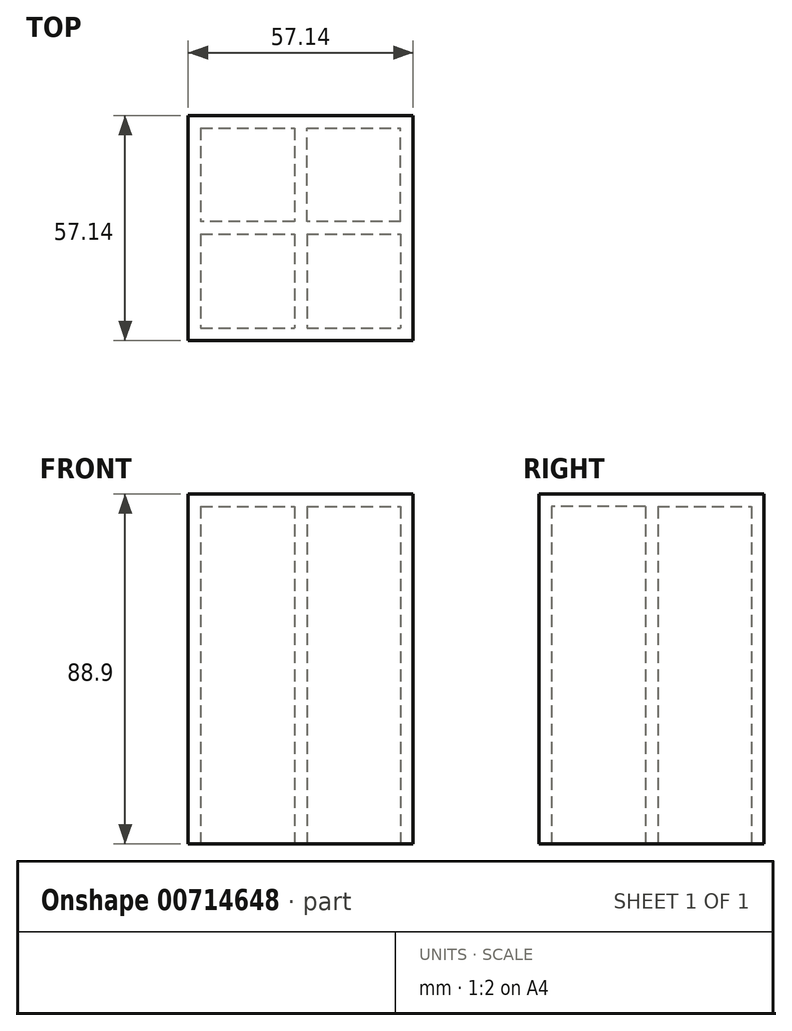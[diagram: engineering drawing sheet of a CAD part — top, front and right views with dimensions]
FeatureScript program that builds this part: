
annotation { "Feature Type Name" : "Feature", "Feature Type Description" : "" }
export const myFeature = defineFeature(function(context is Context, id is Id, definition is map)
    precondition{}
    {
        {
            var Q0;
            Q0=qCreatedBy(makeId("Top.planeOp"),FACE);
            var sketch = newSketch(context, id + "F0", { "sketchPlane" : qUnion([Q0])});
            skLineSegment(sketch, "E0.bottom", {"start": v(28.57, 28.58) * mm, "end": v(-28.58, 28.58) * mm});
            skLineSegment(sketch, "E0.top", {"start": v(28.58, -28.58) * mm, "end": v(-28.57, -28.58) * mm});
            skLineSegment(sketch, "E0.left", {"start": v(28.57, 28.58) * mm, "end": v(28.58, -28.58) * mm});
            skLineSegment(sketch, "E0.right", {"start": v(-28.58, 28.58) * mm, "end": v(-28.57, -28.58) * mm});
            skPoint(sketch, "E0.middle", {"position": v(0, 0) * mm});
            skSolve(sketch);
        }
        {
            var Q0;
            Q0=makeQuery(id+"F0.imprint","IMPRINT",FACE,{"disambiguationData":[TD([[makeQuery(id+"F0.imprint","IMPRINT",EDGE,{"derivedFrom":sQuery(id+"F0.wireOp",EDGE,"E0.bottom")}),1.0]])]});
            extrude(context, id + "F1", {"entities" : qUnion([Q0]), "depth" : 88.9 * mm, "offsetDistance" : 25.4 * mm});
        }
        {
            var Q0;
            Q0=qCreatedBy(makeId("Top.planeOp"),FACE);
            var sketch = newSketch(context, id + "F2", { "sketchPlane" : qUnion([Q0])});
            skLineSegment(sketch, "E1.bottom", {"start": v(-25.4, 25.4) * mm, "end": v(-1.59, 25.4) * mm});
            skLineSegment(sketch, "E1.left", {"start": v(-25.4, 25.4) * mm, "end": v(-25.4, 1.59) * mm});
            skLineSegment(sketch, "E1.right", {"start": v(-1.59, 25.4) * mm, "end": v(-1.59, 1.59) * mm});
            skLineSegment(sketch, "E2.top", {"start": v(1.59, 25.4) * mm, "end": v(25.4, 25.4) * mm});
            skLineSegment(sketch, "E2.left", {"start": v(1.59, 1.59) * mm, "end": v(1.59, 25.4) * mm});
            skLineSegment(sketch, "E2.right", {"start": v(25.4, 1.59) * mm, "end": v(25.4, 25.4) * mm});
            skLineSegment(sketch, "E3.bottom", {"start": v(-25.4, -1.59) * mm, "end": v(-1.59, -1.59) * mm});
            skLineSegment(sketch, "E3.top", {"start": v(-25.4, -25.4) * mm, "end": v(-1.59, -25.4) * mm});
            skLineSegment(sketch, "E3.left", {"start": v(-25.4, -1.59) * mm, "end": v(-25.4, -25.4) * mm});
            skLineSegment(sketch, "E3.right", {"start": v(-1.59, -1.59) * mm, "end": v(-1.59, -25.4) * mm});
            skLineSegment(sketch, "E4.bottom", {"start": v(1.59, -1.59) * mm, "end": v(25.4, -1.59) * mm});
            skLineSegment(sketch, "E4.top", {"start": v(1.59, -25.4) * mm, "end": v(25.4, -25.4) * mm});
            skLineSegment(sketch, "E4.right", {"start": v(25.4, -1.59) * mm, "end": v(25.4, -25.4) * mm});
            skLineSegment(sketch, "E5", {"start": v(25.4, 1.59) * mm, "end": v(1.59, 1.59) * mm});
            skPoint(sketch, "E6.orphan", {"position": v(1.59, 0) * mm});
            skLineSegment(sketch, "E7.trimOffspring", {"start": v(-1.59, 1.59) * mm, "end": v(-25.4, 1.59) * mm});
            skPoint(sketch, "E1.top.end.orphan", {"position": v(-1.59, 0) * mm});
            skLineSegment(sketch, "E8", {"start": v(0, 0) * mm, "end": v(0, 28.84) * mm});
            skLineSegment(sketch, "E9", {"start": v(1.59, -1.59) * mm, "end": v(1.59, -25.4) * mm});
            skSolve(sketch);
        }
        {
            var Q0;
            Q0=makeQuery(id+"F2.imprint","IMPRINT",FACE,{"disambiguationData":[TD([[makeQuery(id+"F2.imprint","IMPRINT",EDGE,{"derivedFrom":sQuery(id+"F2.wireOp",EDGE,"E3.bottom")}),-1.0]])]});
            var Q1;
            Q1=makeQuery(id+"F2.imprint","IMPRINT",FACE,{"disambiguationData":[TD([[makeQuery(id+"F2.imprint","IMPRINT",EDGE,{"derivedFrom":sQuery(id+"F2.wireOp",EDGE,"E4.bottom")}),-1.0]])]});
            var Q2;
            Q2=makeQuery(id+"F2.imprint","IMPRINT",FACE,{"disambiguationData":[TD([[makeQuery(id+"F2.imprint","IMPRINT",EDGE,{"derivedFrom":sQuery(id+"F2.wireOp",EDGE,"E1.bottom")}),-1.0]])]});
            var Q3;
            Q3=makeQuery(id+"F2.imprint","IMPRINT",FACE,{"disambiguationData":[TD([[makeQuery(id+"F2.imprint","IMPRINT",EDGE,{"derivedFrom":sQuery(id+"F2.wireOp",EDGE,"E2.top")}),-1.0]])]});
            extrude(context, id + "F3", {"entities" : qUnion([Q0, Q1, Q2, Q3]), "operationType" : NewBodyOperationType.REMOVE, "depth" : 85.72 * mm, "offsetDistance" : 25.4 * mm});
        }
    });
